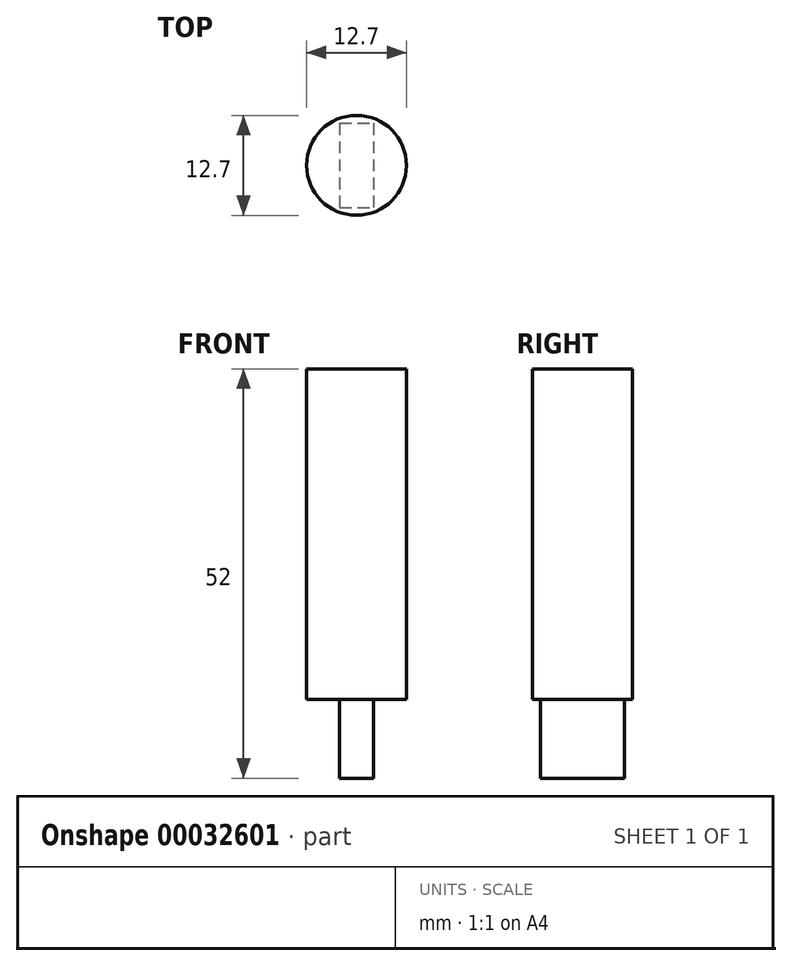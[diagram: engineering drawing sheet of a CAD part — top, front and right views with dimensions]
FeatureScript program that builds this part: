
annotation { "Feature Type Name" : "Feature", "Feature Type Description" : "" }
export const myFeature = defineFeature(function(context is Context, id is Id, definition is map)
    precondition{}
    {
        {
            var Q0;
            Q0=qCreatedBy(makeId("Top.planeOp"),FACE);
            var sketch = newSketch(context, id + "F0", { "sketchPlane" : qUnion([Q0])});
            skCircle(sketch, "E0", {"center": v(0, 0) * mm, "radius": 6.34 * mm});
            skLineSegment(sketch, "E1.rect.bottom", {"start": v(-2.15, 5.35) * mm, "end": v(2.15, 5.35) * mm});
            skLineSegment(sketch, "E1.rect.top", {"start": v(-2.15, -5.35) * mm, "end": v(2.15, -5.35) * mm});
            skLineSegment(sketch, "E1.rect.left", {"start": v(-2.15, 5.35) * mm, "end": v(-2.15, -5.35) * mm});
            skLineSegment(sketch, "E1.rect.right", {"start": v(2.15, 5.35) * mm, "end": v(2.15, -5.35) * mm});
            skSolve(sketch);
        }
        {
            var Q0;
            Q0 = qSketchRegion(id + "F0", true);
            var Q1;
            Q1=makeQuery(id+"F0.imprint","IMPRINT",FACE,{"disambiguationData":[TD([[makeQuery(id+"F0.imprint","IMPRINT",EDGE,{"derivedFrom":sQuery(id+"F0.wireOp",EDGE,"E1.rect.bottom")}),-1.0]])]});
            extrude(context, id + "F1", {"entities" : qUnion([Q0, Q1]), "depth" : 42 * mm});
        }
        {
            var Q0;
            Q0=makeQuery(id+"F0.imprint","IMPRINT",FACE,{"disambiguationData":[TD([[makeQuery(id+"F0.imprint","IMPRINT",EDGE,{"derivedFrom":sQuery(id+"F0.wireOp",EDGE,"E1.rect.bottom")}),-1.0]])]});
            extrude(context, id + "F2", {"entities" : qUnion([Q0]), "operationType" : NewBodyOperationType.ADD, "oppositeDirection" : true, "depth" : 10 * mm});
        }
    });
